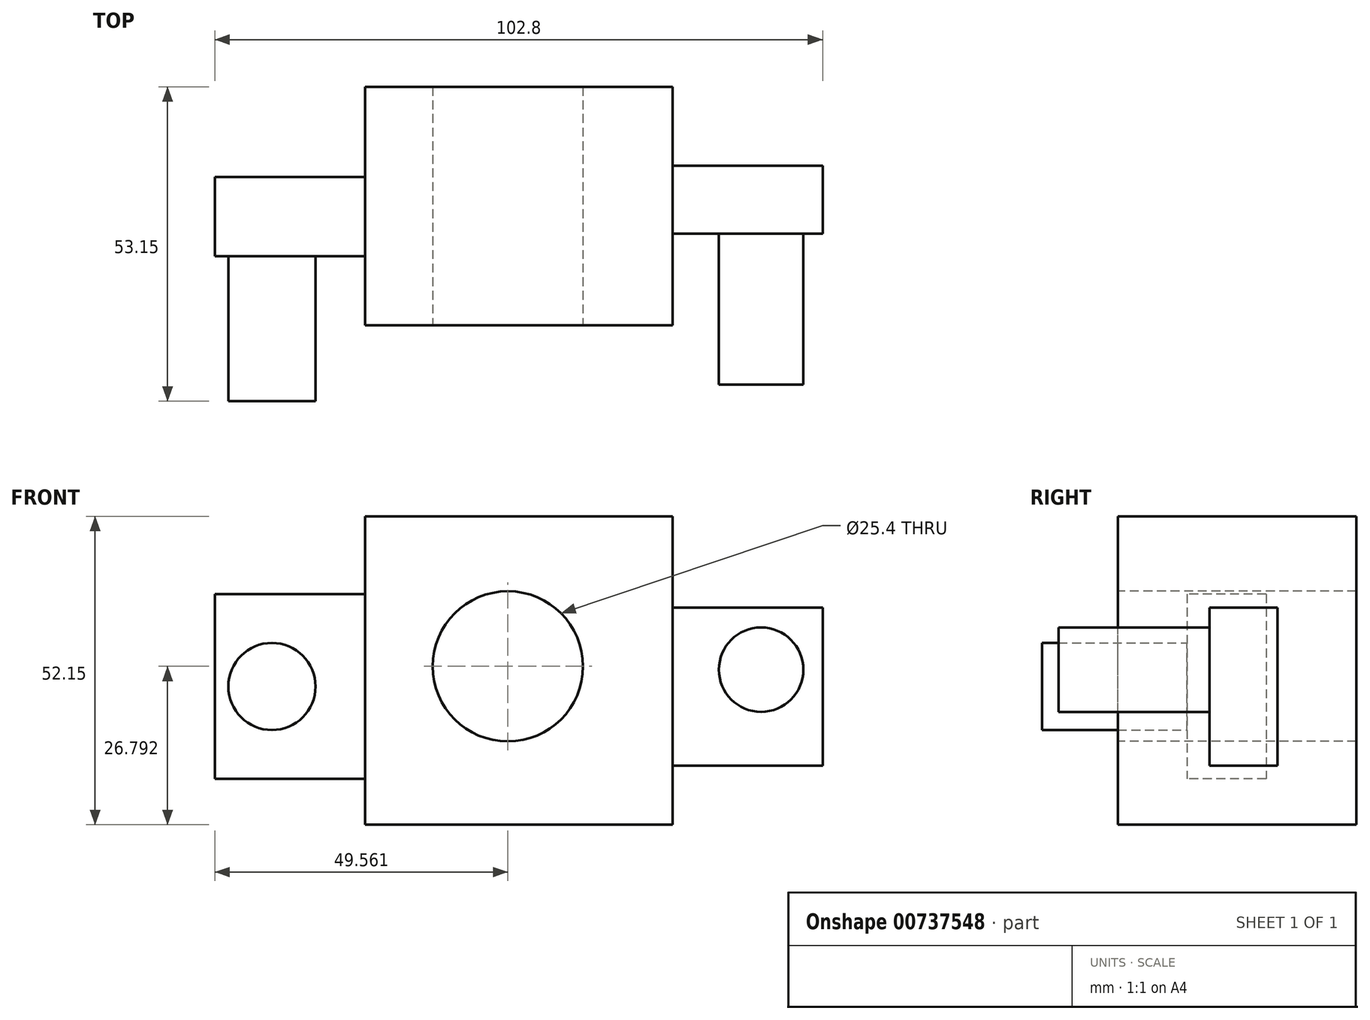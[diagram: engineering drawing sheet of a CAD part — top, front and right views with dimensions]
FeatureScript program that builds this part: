
annotation { "Feature Type Name" : "Feature", "Feature Type Description" : "" }
export const myFeature = defineFeature(function(context is Context, id is Id, definition is map)
    precondition{}
    {
        {
            var Q0;
            Q0=qCreatedBy(makeId("Front.planeOp"),FACE);
            var sketch = newSketch(context, id + "F0", { "sketchPlane" : qUnion([Q0])});
            skLineSegment(sketch, "E0.bottom", {"start": v(19.5, -45.77) * mm, "end": v(-7.09, -45.77) * mm});
            skLineSegment(sketch, "E0.top", {"start": v(19.5, 6.38) * mm, "end": v(-7.09, 6.38) * mm});
            skLineSegment(sketch, "E0.left", {"start": v(19.5, -45.77) * mm, "end": v(19.5, 6.38) * mm});
            skLineSegment(sketch, "E0.right", {"start": v(-7.09, -45.77) * mm, "end": v(-7.09, 6.38) * mm});
            skSolve(sketch);
        }
        {
            var Q0;
            Q0=makeQuery(id+"F0.imprint","IMPRINT",FACE,{"disambiguationData":[TD([[makeQuery(id+"F0.imprint","IMPRINT",EDGE,{"derivedFrom":sQuery(id+"F0.wireOp",EDGE,"E0.bottom")}),-1.0]])]});
            extrude(context, id + "F1", {"entities" : qUnion([Q0]), "depth" : 25.4 * mm, "offsetDistance" : 25.4 * mm});
        }
        {
            var Q0;
            Q0=makeQuery(id+"F1.opExtrude","SWEPT_FACE",FACE,{"disambiguationData":[OSD([sQuery(id+"F0.wireOp",EDGE,"E0.left")])]});
            extrude(context, id + "F2", {"entities" : qUnion([Q0]), "operationType" : NewBodyOperationType.ADD, "depth" : 25.4 * mm, "offsetDistance" : 25.4 * mm});
        }
        {
            var Q0;
            {var subQ0=sQuery(id+"F0.wireOp",EDGE,"E0.left");Q0=makeQuery(id+"F2.boolean.opBoolean","MERGE",FACE,{"derivedFrom":[makeQuery(id+"F1.opExtrude","CAP_FACE",FACE,{"disambiguationData":[OSD([sQuery(id+"F0.wireOp",EDGE,"E0.bottom"),sQuery(id+"F0.wireOp",EDGE,"E0.top"),subQ0,sQuery(id+"F0.wireOp",EDGE,"E0.right")])],"isStart":false}),makeQuery(id+"F2.opExtrude","SWEPT_FACE",FACE,{"disambiguationData":[OSD([subQ0]),TDD([makeQuery(id+"F1.opExtrude","CAP_EDGE",EDGE,{"disambiguationData":[OSD([subQ0])],"isStart":false})])]})]});}
            extrude(context, id + "F3", {"entities" : qUnion([Q0]), "operationType" : NewBodyOperationType.ADD, "depth" : 14.93 * mm, "offsetDistance" : 25.4 * mm});
        }
        {
            var Q0;
            Q0=makeQuery(id+"F3.opExtrude","CAP_FACE",FACE,{"disambiguationData":[OSD([sQuery(id+"F0.wireOp",EDGE,"E0.bottom"),sQuery(id+"F0.wireOp",EDGE,"E0.top"),sQuery(id+"F0.wireOp",EDGE,"E0.left"),sQuery(id+"F0.wireOp",EDGE,"E0.right")])],"isStart":false});
            var sketch = newSketch(context, id + "F4", { "sketchPlane" : qUnion([Q0])});
            skSolve(sketch);
        }
        {
            var Q0;
            Q0=makeQuery(id+"F4.imprint","IMPRINT",FACE,{"disambiguationData":[TD([[makeQuery(id+"F4.imprint","IMPRINT",EDGE,{"derivedFrom":makeQuery(id+"F3.opExtrude","CAP_EDGE",EDGE,{"disambiguationData":[OSD([sQuery(id+"F0.wireOp",EDGE,"E0.right")])],"isStart":false})}),-1.0]])]});
            var sketch = newSketch(context, id + "F5", { "sketchPlane" : qUnion([Q0])});
            skPoint(sketch, "E1", {"position": v(17.07, -18.98) * mm});
            skSolve(sketch);
        }
        {
            var Q0;
            Q0=sQuery(id+"F5.wireOp",VERTEX,"E1");
            var Q1;
            Q1=makeQuery(id+"F1.opExtrude","SWEPT_BODY",BODY,{"disambiguationData":[OSD([sQuery(id+"F0.wireOp",EDGE,"E0.bottom"),sQuery(id+"F0.wireOp",EDGE,"E0.top"),sQuery(id+"F0.wireOp",EDGE,"E0.left"),sQuery(id+"F0.wireOp",EDGE,"E0.right")])]});
            hole(context, id + "F6", {"style" : HoleStyle.SIMPLE, "endStyle" : HoleEndStyle.THROUGH, "holeDiameter" : 25.4 * mm, "majorDiameter" : 6.35 * mm, "isTappedThrough" : true, "tappedDepth" : 12.7 * mm, "tapClearance" : 3, "locations" : qUnion([Q0]), "scope" : qUnion([Q1])});
        }
        {
            var Q0;
            {var subQ0=sQuery(id+"F0.wireOp",EDGE,"E0.left");Q0=makeQuery(id+"F3.boolean.opBoolean","MERGE",FACE,{"derivedFrom":[makeQuery(id+"F2.opExtrude","CAP_FACE",FACE,{"disambiguationData":[OSD([subQ0])],"isStart":false}),makeQuery(id+"F3.opExtrude","SWEPT_FACE",FACE,{"disambiguationData":[OSD([subQ0])]})]});}
            var sketch = newSketch(context, id + "F7", { "sketchPlane" : qUnion([Q0])});
            skPoint(sketch, "E2", {"position": v(-18.34, -20.61) * mm});
            skSolve(sketch);
        }
        {
            var Q0;
            {var subQ0=sQuery(id+"F0.wireOp",EDGE,"E0.left");Q0=makeQuery(id+"F7.imprint","IMPRINT",FACE,{"disambiguationData":[TD([[makeQuery(id+"F7.imprint","IMPRINT",EDGE,{"derivedFrom":makeQuery(id+"F3.opExtrude","CAP_EDGE",EDGE,{"disambiguationData":[OSD([subQ0])],"isStart":false})}),-1.0]])]});}
            var sketch = newSketch(context, id + "F8", { "sketchPlane" : qUnion([Q0])});
            skLineSegment(sketch, "E3.bottom", {"start": v(-24.8, -9.07) * mm, "end": v(-13.31, -9.07) * mm});
            skLineSegment(sketch, "E3.top", {"start": v(-24.8, -35.77) * mm, "end": v(-13.31, -35.77) * mm});
            skLineSegment(sketch, "E3.left", {"start": v(-24.8, -9.07) * mm, "end": v(-24.8, -35.77) * mm});
            skLineSegment(sketch, "E3.right", {"start": v(-13.31, -9.07) * mm, "end": v(-13.31, -35.77) * mm});
            skPoint(sketch, "E3.middle", {"position": v(-19.06, -22.42) * mm});
            skSolve(sketch);
        }
        {
            var Q0;
            Q0 = qSketchRegion(id + "F8", true);
            extrude(context, id + "F9", {"entities" : qUnion([Q0]), "operationType" : NewBodyOperationType.ADD, "depth" : 25.4 * mm, "offsetDistance" : 25.4 * mm});
        }
        {
            var Q0;
            {var subQ0=sQuery(id+"F0.wireOp",EDGE,"E0.right");Q0=makeQuery(id+"F3.boolean.opBoolean","MERGE",FACE,{"derivedFrom":[makeQuery(id+"F1.opExtrude","SWEPT_FACE",FACE,{"disambiguationData":[OSD([subQ0])]}),makeQuery(id+"F3.opExtrude","SWEPT_FACE",FACE,{"disambiguationData":[OSD([subQ0])]})]});}
            var sketch = newSketch(context, id + "F10", { "sketchPlane" : qUnion([Q0])});
            skLineSegment(sketch, "E4.bottom", {"start": v(15.26, -6.76) * mm, "end": v(28.62, -6.76) * mm});
            skLineSegment(sketch, "E4.top", {"start": v(15.26, -37.98) * mm, "end": v(28.62, -37.98) * mm});
            skLineSegment(sketch, "E4.left", {"start": v(15.26, -6.76) * mm, "end": v(15.26, -37.98) * mm});
            skLineSegment(sketch, "E4.right", {"start": v(28.62, -6.76) * mm, "end": v(28.62, -37.98) * mm});
            skPoint(sketch, "E4.middle", {"position": v(21.94, -22.37) * mm});
            skSolve(sketch);
        }
        {
            var Q0;
            Q0 = qSketchRegion(id + "F10", true);
            extrude(context, id + "F11", {"entities" : qUnion([Q0]), "operationType" : NewBodyOperationType.ADD, "depth" : 25.4 * mm, "offsetDistance" : 25.4 * mm});
        }
        {
            var Q0;
            Q0=makeQuery(id+"F9.opExtrude","SWEPT_FACE",FACE,{"disambiguationData":[OSD([sQuery(id+"F8.wireOp",EDGE,"E3.left")])]});
            var sketch = newSketch(context, id + "F12", { "sketchPlane" : qUnion([Q0])});
            skCircle(sketch, "E5", {"center": v(59.9, -19.54) * mm, "radius": 7.14 * mm});
            skSolve(sketch);
        }
        {
            var Q0;
            Q0 = qSketchRegion(id + "F12", true);
            extrude(context, id + "F13", {"entities" : qUnion([Q0]), "operationType" : NewBodyOperationType.ADD, "depth" : 25.56 * mm, "offsetDistance" : 25.4 * mm});
        }
        {
            var Q0;
            Q0=makeQuery(id+"F11.opExtrude","SWEPT_FACE",FACE,{"disambiguationData":[OSD([sQuery(id+"F10.wireOp",EDGE,"E4.right")])]});
            var sketch = newSketch(context, id + "F14", { "sketchPlane" : qUnion([Q0])});
            skCircle(sketch, "E6", {"center": v(-22.83, -22.38) * mm, "radius": 7.37 * mm});
            skSolve(sketch);
        }
        {
            var Q0;
            Q0 = qSketchRegion(id + "F14", true);
            extrude(context, id + "F15", {"entities" : qUnion([Q0]), "operationType" : NewBodyOperationType.ADD, "depth" : 24.53 * mm, "offsetDistance" : 25.4 * mm});
        }
    });
